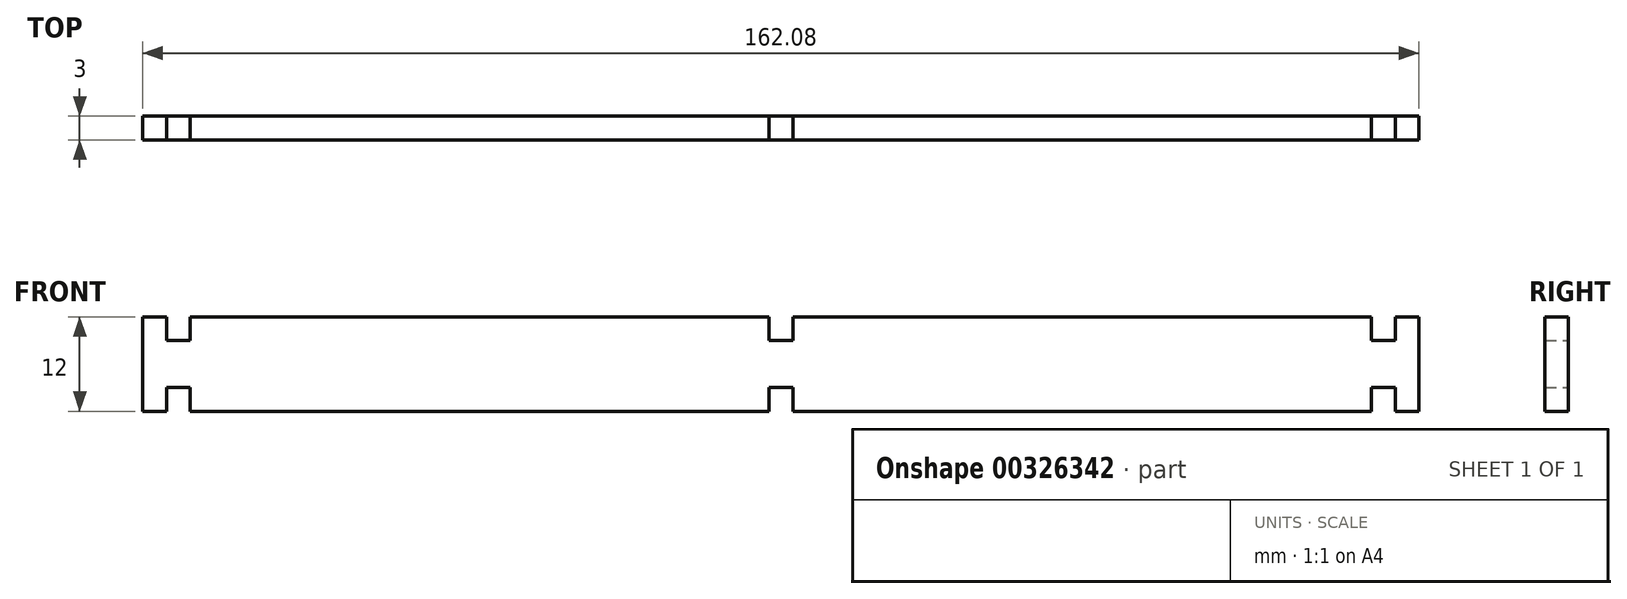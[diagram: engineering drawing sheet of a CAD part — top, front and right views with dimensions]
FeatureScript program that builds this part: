
annotation { "Feature Type Name" : "Feature", "Feature Type Description" : "" }
export const myFeature = defineFeature(function(context is Context, id is Id, definition is map)
    precondition{}
    {
        {
            var Q0;
            Q0=qCreatedBy(makeId("Front.planeOp"),FACE);
            var sketch = newSketch(context, id + "F0", { "sketchPlane" : qUnion([Q0])});
            skPoint(sketch, "E0", {"position": v(-78.04, 0) * mm});
            skPoint(sketch, "E1", {"position": v(-78.04, 3.02) * mm});
            skPoint(sketch, "E2", {"position": v(-75, 3.02) * mm});
            skPoint(sketch, "E3", {"position": v(78.04, 0) * mm});
            skPoint(sketch, "E4", {"position": v(78.04, 3.02) * mm});
            skPoint(sketch, "E5", {"position": v(75, 3.02) * mm});
            skPoint(sketch, "E6", {"position": v(75, 0) * mm});
            skLineSegment(sketch, "E7", {"start": v(-78.04, 0) * mm, "end": v(-78.04, 3.02) * mm});
            skLineSegment(sketch, "E8", {"start": v(-75, 3.02) * mm, "end": v(-78.04, 3.02) * mm});
            skLineSegment(sketch, "E9", {"start": v(-75, 0) * mm, "end": v(-75, 3.02) * mm});
            skLineSegment(sketch, "E10", {"start": v(75, 0) * mm, "end": v(75, 3.02) * mm});
            skLineSegment(sketch, "E11", {"start": v(78.04, 3.02) * mm, "end": v(75, 3.02) * mm});
            skLineSegment(sketch, "E12", {"start": v(78.04, 0) * mm, "end": v(78.04, 3.02) * mm});
            skLineSegment(sketch, "E13.trimOffspring", {"start": v(78.04, 0) * mm, "end": v(81.04, 0) * mm});
            skLineSegment(sketch, "E14.trimOffspring", {"start": v(-78.04, 0) * mm, "end": v(-81.04, 0) * mm});
            skLineSegment(sketch, "E15", {"start": v(-81.04, 12) * mm, "end": v(-78.04, 12) * mm});
            skLineSegment(sketch, "E16", {"start": v(-78.04, 12) * mm, "end": v(-78.04, 8.98) * mm});
            skLineSegment(sketch, "E17", {"start": v(-78.04, 8.98) * mm, "end": v(-75, 8.98) * mm});
            skLineSegment(sketch, "E18", {"start": v(-75, 8.98) * mm, "end": v(-75, 12) * mm});
            skLineSegment(sketch, "E19", {"start": v(81.04, 12) * mm, "end": v(78.04, 12) * mm});
            skLineSegment(sketch, "E20", {"start": v(78.04, 12) * mm, "end": v(78.04, 8.98) * mm});
            skLineSegment(sketch, "E21", {"start": v(78.04, 8.98) * mm, "end": v(75, 8.98) * mm});
            skLineSegment(sketch, "E22", {"start": v(75, 8.98) * mm, "end": v(75, 12) * mm});
            skLineSegment(sketch, "E23", {"start": v(75, 12) * mm, "end": v(1.52, 12) * mm});
            skLineSegment(sketch, "E24", {"start": v(81.04, 12) * mm, "end": v(81.04, 0) * mm});
            skLineSegment(sketch, "E25", {"start": v(-81.04, 12) * mm, "end": v(-81.04, 0) * mm});
            skLineSegment(sketch, "E26", {"start": v(-75, 0) * mm, "end": v(-1.52, 0) * mm});
            skLineSegment(sketch, "E27", {"start": v(-1.52, 12) * mm, "end": v(-1.52, 8.98) * mm});
            skLineSegment(sketch, "E28", {"start": v(1.52, 12) * mm, "end": v(1.52, 8.98) * mm});
            skLineSegment(sketch, "E29", {"start": v(-1.52, 0) * mm, "end": v(-1.52, 3.02) * mm});
            skLineSegment(sketch, "E30", {"start": v(1.52, 0) * mm, "end": v(1.52, 3.02) * mm});
            skLineSegment(sketch, "E31", {"start": v(-1.52, 3.02) * mm, "end": v(1.52, 3.02) * mm});
            skLineSegment(sketch, "E32", {"start": v(-1.52, 8.98) * mm, "end": v(1.52, 8.98) * mm});
            skLineSegment(sketch, "E33.trimOffspring", {"start": v(-1.52, 12) * mm, "end": v(-75, 12) * mm});
            skLineSegment(sketch, "E34.trimOffspring", {"start": v(1.52, 0) * mm, "end": v(75, 0) * mm});
            skSolve(sketch);
        }
        {
            var Q0;
            Q0=makeQuery(id+"F0.imprint","IMPRINT",FACE,{"disambiguationData":[TD([[makeQuery(id+"F0.imprint","IMPRINT",EDGE,{"derivedFrom":sQuery(id+"F0.wireOp",EDGE,"ItmVC9ZI-ysAT-GvL9-55L5-KoOHRsY66XSg")}),-1.0]])]});
            var Q1;
            Q1=makeQuery(id+"F0.imprint","IMPRINT",FACE,{"disambiguationData":[TD([[makeQuery(id+"F0.imprint","IMPRINT",EDGE,{"derivedFrom":sQuery(id+"F0.wireOp",EDGE,"E7")}),1.0]])]});
            extrude(context, id + "F1", {"entities" : qUnion([Q0, Q1]), "depth" : 3 * mm});
        }
    });
